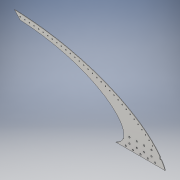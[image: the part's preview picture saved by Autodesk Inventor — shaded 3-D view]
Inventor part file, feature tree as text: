
AUTODESK INVENTOR PART (.ipt)
format: ipt  version: 2016 (Build 200138000, 138)  size: 398,336 bytes
history: native  units: in
note: dims shown in document units (in); Inventor stores cm internally (conversion verified against a paired STEP export)
features: other x15, sketch x8, projected_geometry x4, sheet_metal_op x1, pattern_linear x1
ambient origin geometry x8: Origin, YZ Plane, XZ Plane, XY Plane, X Axis, Y Axis, Z Axis, Center Point
bodies: Solid1 (feature_tree)
feature tree (29):
  other  "UCS1"
  sheet_metal_op  "Face1"
  other  "A-Side Definition"
  sketch  "Sketch6"  dims[d7=0.12in]
  pattern_linear  "Rectangular Pattern1"  Count1=100  [1 undecoded]
  sketch  "Sketch10"  dims[d11=1.5748in]
  sketch  "Sketch12"  dims[d12=0.5in]
  sketch  "Sketch13"  dims[d16=0.4173in d17=1.1811in d19=2.0in d20=0.3937in d22=1.0in d24=1.1811in d26=2.0in d27=0.3937in d29=1.0in d31=0.12in d32=0.0in d33=0.5906in d34=1.9685in d35=0.12in d36=0.0in d37=0.4173in d38=1.0in d39=1.1811in d41=2.0in d42=0.3937in d44=1.0in d46=0.7874in d48=2.0in d49=0.3937in d51=1.0in d53=0.2598in d54=0.12in d55=0.0in d56=12.5984in d58=1.25in d59=0.4724in d60=0.4173in d61=1.5748in d63=2.0in d64=0.3937in d66=1.0in d68=0.12in d69=0.0in d70=0.0in d71=0.0in d72=0.0in d73=0.0in d74=0.0in d75=-0.6184in d79=1.25in]
  other  "Plate1"
  sketch  "Sketch3"  dims[d5=0.5978in]
  projected_geometry  "Projected Loop1"
  sketch  "Sketch4"  dims[d6=1.5748in]
  sketch  "Sketch7"  dims[d9=17.3228in]
  sketch  "Sketch8"  dims[d10=0.0in]
  projected_geometry  "Projected Loop2"
  projected_geometry  "Projected Loop4"
  other  "Cut2"
  other  "Cut3"
  other  "Cut4"
  other  "Cut5"
  other  "UCS1: YZ Plane"
  other  "UCS1: XZ Plane"
  other  "UCS1: XY Plane"
  other  "UCS1: X Axis"
  other  "UCS1: Y Axis"
  other  "UCS1: Z Axis"
  other  "UCS1: Center Point"
  projected_geometry  "Project Cut Edges1"
  other  "Definition1"
note: 1 required parameter value undecoded (feature->parameter linkage not recoverable at this tier; creation-order binding heuristic only, values carry confidence <= 0.55)
